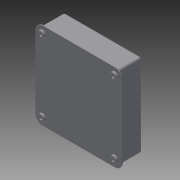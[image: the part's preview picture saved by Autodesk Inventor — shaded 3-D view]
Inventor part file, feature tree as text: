
AUTODESK INVENTOR PART (.ipt)
format: ipt  version: 2013 (Build 170138000, 138)  size: 300,544 bytes
history: native  units: mm
features: sketch x5, extrude x4, other x3, fillet x2, hole x1, chamfer x1
ambient origin geometry x8: Origin, YZ Plane, XZ Plane, XY Plane, X Axis, Y Axis, Z Axis, Center Point
feature tree (16):
  other  "ソリッド1"
  extrude  "押し出し1"  Depth=120.0mm
  extrude  "押し出し2"  Depth=120.0mm
  hole  "穴1"  [1 undecoded]
  fillet  "フィレット1"  Radius=60.0mm
  extrude  "押し出し3"  Depth=1.0mm TaperAngle=0.0deg
  fillet  "フィレット2"  Radius=4.0mm
  extrude  "押し出し4"  Depth=100.0mm
  chamfer  "面取り1"  Distance=100.0mm
  sketch  "スケッチ1"
  sketch  "スケッチ2"
  sketch  "スケッチ3"
  sketch  "スケッチ4"
  sketch  "スケッチ5"
  other  "断面エッジを投影1"
  other  "断面エッジを投影2"
note: 1 required parameter value undecoded (feature->parameter linkage not recoverable at this tier; creation-order binding heuristic only, values carry confidence <= 0.55)
